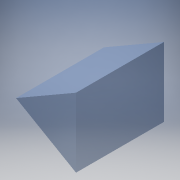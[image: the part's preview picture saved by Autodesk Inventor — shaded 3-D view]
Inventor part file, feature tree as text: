
AUTODESK INVENTOR PART (.ipt)
format: ipt  version: 2017 (Build 210142000, 142)  size: 94,720 bytes
history: native  units: mm
features: extrude x1, sketch x1
ambient origin geometry x8: Origin, YZ Plane, XZ Plane, XY Plane, X Axis, Y Axis, Z Axis, Center Point
bodies: Solid1 (feature_tree)
feature tree (2):
  extrude  "Extrusion1"  Depth=10.0mm TaperAngle=0.0deg
  sketch  "Sketch1"  dims[d0=10.0mm d1=10.0mm d2=0.0mm]
